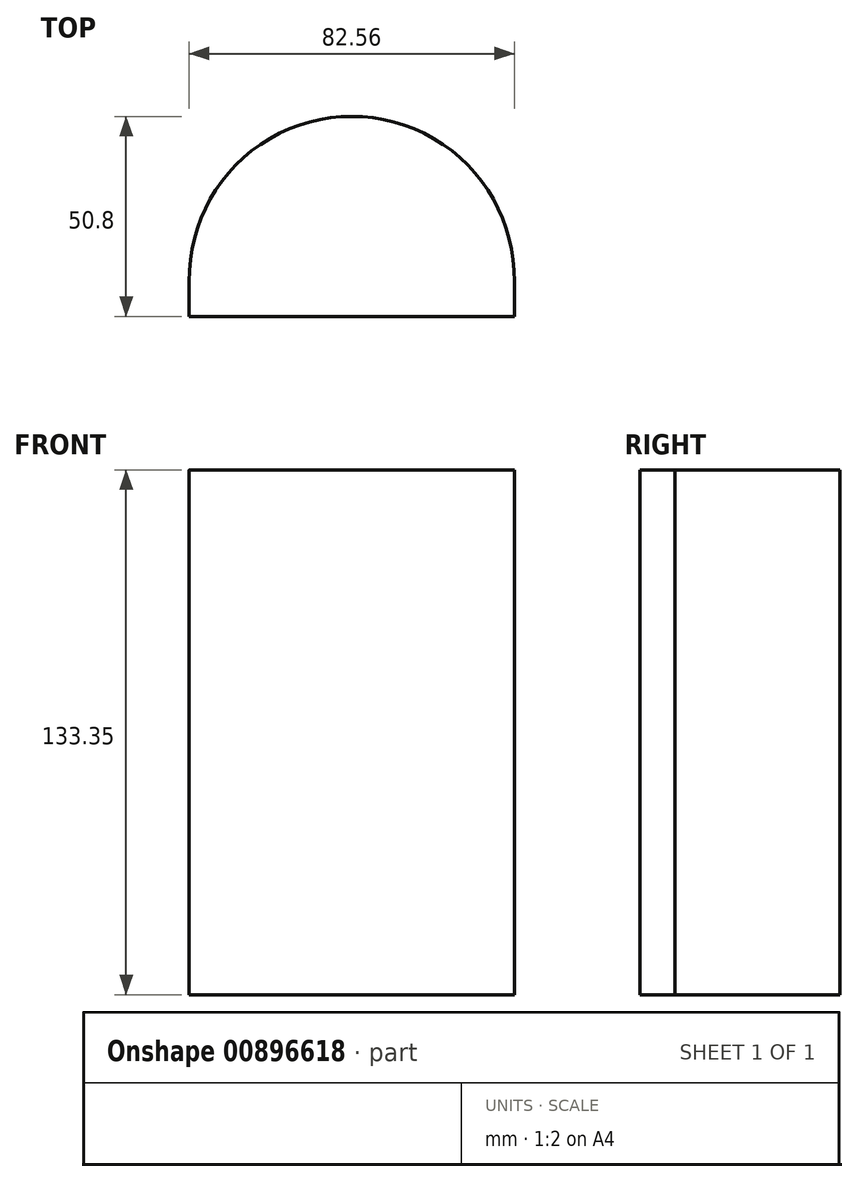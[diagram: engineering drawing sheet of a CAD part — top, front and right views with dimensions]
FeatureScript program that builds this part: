
annotation { "Feature Type Name" : "Feature", "Feature Type Description" : "" }
export const myFeature = defineFeature(function(context is Context, id is Id, definition is map)
    precondition{}
    {
        {
            var Q0;
            Q0=qCreatedBy(makeId("Top.planeOp"),FACE);
            var sketch = newSketch(context, id + "F0", { "sketchPlane" : qUnion([Q0])});
            skLineSegment(sketch, "E0.bottom", {"start": v(-0.06, -9.47) * mm, "end": v(41.22, -9.47) * mm});
            skLineSegment(sketch, "E0.left", {"start": v(-0.06, -9.47) * mm, "end": v(-0.06, 41.33) * mm});
            skLineSegment(sketch, "E0.right", {"start": v(41.22, -9.47) * mm, "end": v(41.22, -0.58) * mm});
            skArc(sketch, "E1", {"start": v(41.22, -0.58) * mm, "mid": v(29.35, 29.01) * mm, "end": v(-0.06, 41.33) * mm});
            skSolve(sketch);
        }
        {
            var Q0;
            Q0=makeQuery(id+"F0.imprint","IMPRINT",FACE,{"disambiguationData":[TD([[makeQuery(id+"F0.imprint","IMPRINT",EDGE,{"derivedFrom":sQuery(id+"F0.wireOp",EDGE,"E0.bottom")}),1.0]])]});
            extrude(context, id + "F1", {"entities" : qUnion([Q0]), "depth" : 133.35 * mm, "offsetDistance" : 25.4 * mm});
        }
        {
            var Q0;
            Q0=makeQuery(id+"F1.opExtrude","SWEPT_BODY",BODY,{"disambiguationData":[OSD([sQuery(id+"F0.wireOp",EDGE,"E0.bottom"),sQuery(id+"F0.wireOp",EDGE,"E0.left"),sQuery(id+"F0.wireOp",EDGE,"E0.right"),sQuery(id+"F0.wireOp",EDGE,"E1")])]});
            var Q1;
            Q1=makeQuery(id+"F1.opExtrude","SWEPT_FACE",FACE,{"disambiguationData":[OSD([sQuery(id+"F0.wireOp",EDGE,"E0.left")])]});
            mirror(context, id + "F2", {"operationType" : NewBodyOperationType.ADD, "entities" : qUnion([Q0]), "mirrorPlane" : qUnion([Q1])});
        }
    });
